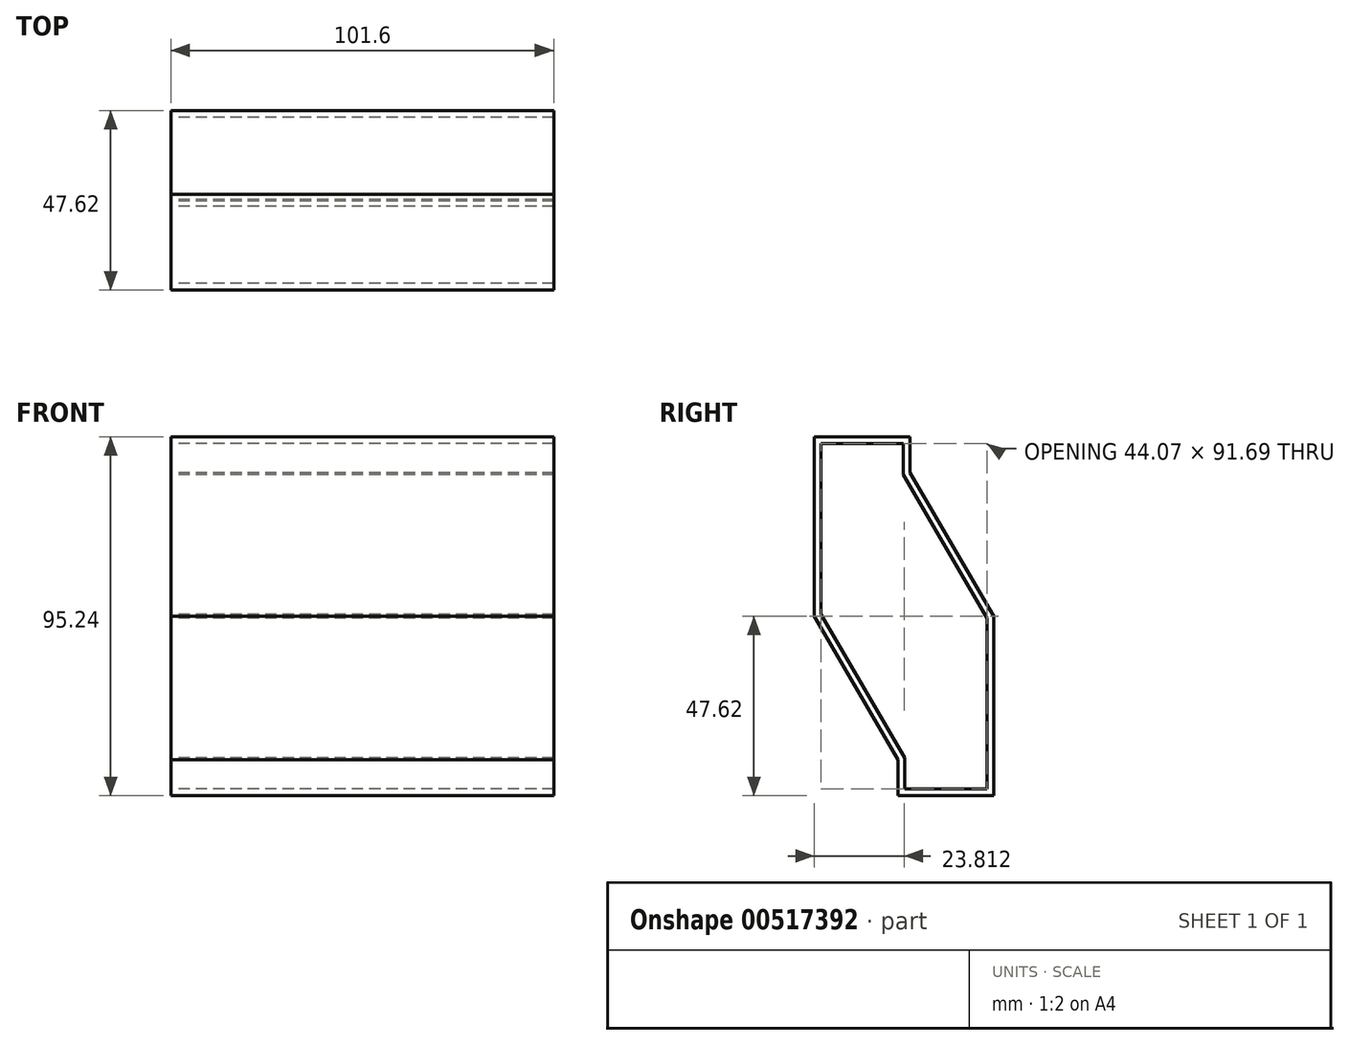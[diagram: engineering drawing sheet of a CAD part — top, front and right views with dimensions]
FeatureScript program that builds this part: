
annotation { "Feature Type Name" : "Feature", "Feature Type Description" : "" }
export const myFeature = defineFeature(function(context is Context, id is Id, definition is map)
    precondition{}
    {
        {
            var Q0;
            Q0=qCreatedBy(makeId("Right.planeOp"),FACE);
            var sketch = newSketch(context, id + "F0", { "sketchPlane" : qUnion([Q0])});
            skLineSegment(sketch, "E0", {"start": v(0, 47.63) * mm, "end": v(0, 0) * mm});
            skLineSegment(sketch, "E1", {"start": v(0, 0) * mm, "end": v(22.23, -38.1) * mm});
            skLineSegment(sketch, "E2", {"start": v(22.23, -38.1) * mm, "end": v(22.23, -47.62) * mm});
            skLineSegment(sketch, "E3", {"start": v(22.23, -47.62) * mm, "end": v(47.63, -47.62) * mm});
            skLineSegment(sketch, "E4", {"start": v(47.63, -47.62) * mm, "end": v(47.63, 0) * mm});
            skLineSegment(sketch, "E5", {"start": v(47.62, 0) * mm, "end": v(25.4, 38.1) * mm});
            skLineSegment(sketch, "E6", {"start": v(25.4, 38.1) * mm, "end": v(25.4, 47.63) * mm});
            skLineSegment(sketch, "E7", {"start": v(25.4, 47.63) * mm, "end": v(0, 47.63) * mm});
            skSolve(sketch);
        }
        {
            var Q0;
            Q0 = qSketchRegion(id + "F0", true);
            extrude(context, id + "F1", {"entities" : qUnion([Q0]), "depth" : 101.6 * mm, "offsetDistance" : 25.4 * mm});
        }
        {
            var Q0;
            Q0=makeQuery(id+"F1.opExtrude","CAP_FACE",FACE,{"disambiguationData":[OSD([sQuery(id+"F0.wireOp",EDGE,"E0"),sQuery(id+"F0.wireOp",EDGE,"E1"),sQuery(id+"F0.wireOp",EDGE,"E2"),sQuery(id+"F0.wireOp",EDGE,"E3"),sQuery(id+"F0.wireOp",EDGE,"E4"),sQuery(id+"F0.wireOp",EDGE,"E5"),sQuery(id+"F0.wireOp",EDGE,"E6"),sQuery(id+"F0.wireOp",EDGE,"E7")])],"isStart":false});
            var Q1;
            Q1=makeQuery(id+"F1.opExtrude","CAP_FACE",FACE,{"disambiguationData":[OSD([sQuery(id+"F0.wireOp",EDGE,"E0"),sQuery(id+"F0.wireOp",EDGE,"E1"),sQuery(id+"F0.wireOp",EDGE,"E2"),sQuery(id+"F0.wireOp",EDGE,"E3"),sQuery(id+"F0.wireOp",EDGE,"E4"),sQuery(id+"F0.wireOp",EDGE,"E5"),sQuery(id+"F0.wireOp",EDGE,"E6"),sQuery(id+"F0.wireOp",EDGE,"E7")])],"isStart":true});
            shell(context, id + "F2", {"entities" : qUnion([Q0, Q1]), "thickness" : 1.78 * mm});
        }
    });
